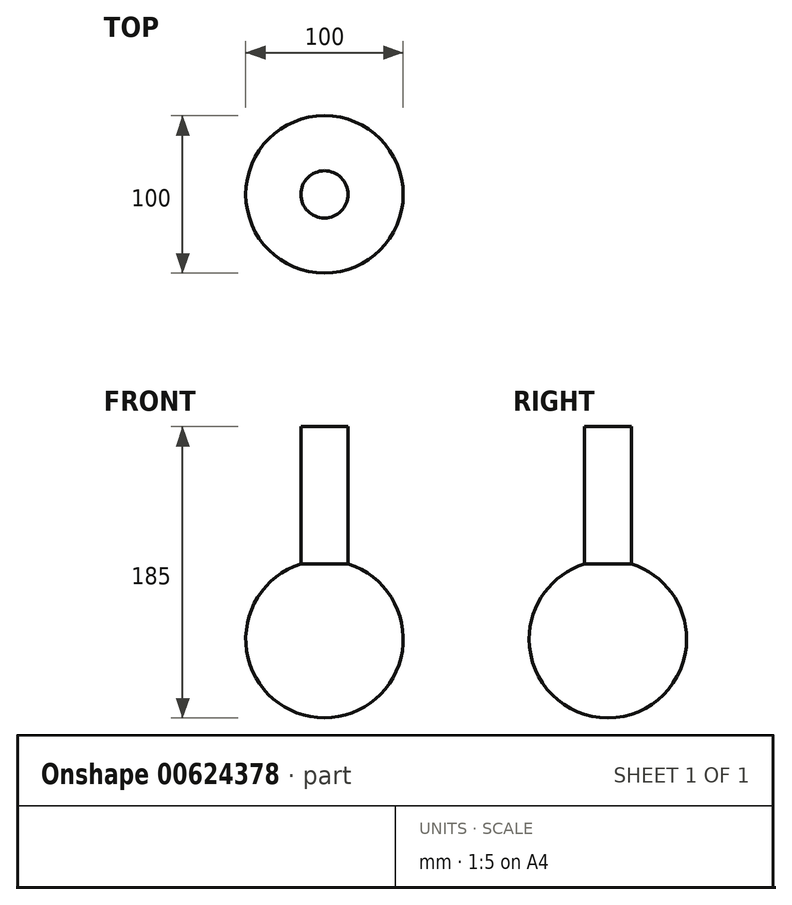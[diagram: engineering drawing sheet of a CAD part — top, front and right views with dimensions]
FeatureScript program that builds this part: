
annotation { "Feature Type Name" : "Feature", "Feature Type Description" : "" }
export const myFeature = defineFeature(function(context is Context, id is Id, definition is map)
    precondition{}
    {
        {
            var Q0;
            Q0=qCreatedBy(makeId("Front.planeOp"),FACE);
            var sketch = newSketch(context, id + "F0", { "sketchPlane" : qUnion([Q0])});
            skCircle(sketch, "E0", {"center": v(0, 0) * mm, "radius": 50 * mm});
            skSolve(sketch);
        }
        {
            var Q0;
            Q0=makeQuery(id+"F0.imprint","IMPRINT",FACE,{"disambiguationData":[TD([[makeQuery(id+"F0.imprint","IMPRINT",EDGE,{"derivedFrom":sQuery(id+"F0.wireOp",EDGE,"E0")}),1.0]])]});
            extrude(context, id + "F1", {"entities" : qUnion([Q0]), "endBound" : BoundingType.SYMMETRIC, "depth" : 100 * mm, "offsetDistance" : 25 * mm});
        }
        {
            var Q0;
            Q0=makeQuery(id+"F1.opExtrude","CAP_FACE",FACE,{"disambiguationData":[OSD([sQuery(id+"F0.wireOp",EDGE,"E0")])],"isStart":false});
            var Q1;
            Q1=makeQuery(id+"F1.opExtrude","CAP_FACE",FACE,{"disambiguationData":[OSD([sQuery(id+"F0.wireOp",EDGE,"E0")])],"isStart":true});
            fillet(context, id + "F2", {"entities" : qUnion([Q0, Q1]), "radius" : 50 * mm, "tangentPropagation" : true, "allowEdgeOverflow" : false});
        }
        {
            var Q0;
            Q0=qCreatedBy(makeId("Top.planeOp"),FACE);
            var sketch = newSketch(context, id + "F3", { "sketchPlane" : qUnion([Q0])});
            skCircle(sketch, "E1", {"center": v(0, 0) * mm, "radius": 15 * mm});
            skSolve(sketch);
        }
        {
            var Q0;
            Q0 = qSketchRegion(id + "F3", true);
            extrude(context, id + "F4", {"entities" : qUnion([Q0]), "operationType" : NewBodyOperationType.ADD, "depth" : 135 * mm, "offsetDistance" : 25 * mm});
        }
    });
